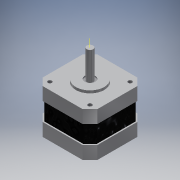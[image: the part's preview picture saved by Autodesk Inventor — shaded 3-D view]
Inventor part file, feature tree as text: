
AUTODESK INVENTOR PART (.ipt)
format: ipt  version: 2017 (Build 210142000, 142)  size: 289,792 bytes
history: native  units: mm
features: sketch x10, extrude x9, projected_geometry x8, mirror x4, plane x4, hole x1, other x1
ambient origin geometry x8: Origin, YZ Plane, XZ Plane, XY Plane, X Axis, Y Axis, Z Axis, Center Point
bodies: Solid1 (feature_tree)
feature tree (37):
  extrude  "Extrusion1"  Depth=40.3mm
  extrude  "Extrusion3"  Depth=34.0mm TaperAngle=0.0deg
  extrude  "Extrusion4"  Depth=2.0mm TaperAngle=0.0deg
  extrude  "Extrusion5"  Depth=1.0mm TaperAngle=0.0deg
  extrude  "Extrusion6"  Depth=22.0mm TaperAngle=0.0deg
  mirror  "Mirror1"
  extrude  "Extrusion7"  Depth=10.0mm
  mirror  "Mirror2"
  extrude  "Extrusion8"  Depth=10.0mm
  extrude  "Extrusion9"  Depth=10.0mm
  sketch  "Sketch15"  dims[d44=10.0mm d45=1.0mm d46=0.0mm]
  extrude  "Extrusion10"  Depth=1.0mm TaperAngle=0.0deg
  mirror  "Mirror3"
  mirror  "Mirror4"
  hole  "Hole3"  [1 undecoded]
  plane  "Work Plane4"
  sketch  "Sketch2"  dims[d2=30.0mm d3=40.3mm]
  sketch  "Sketch7"  dims[d4=135.0deg d5=34.0mm d6=0.0mm]
  sketch  "Sketch8"  dims[d27=22.0mm d28=2.0mm d29=0.0mm]
  sketch  "Sketch9"  dims[d30=8.0mm d31=1.0mm d32=0.0mm]
  sketch  "Sketch10"  dims[d33=5.0mm d34=22.0mm d35=0.0mm]
  projected_geometry  "Projected Loop2"
  sketch  "Sketch11"  dims[d36=10.0mm d37=10.0mm]
  projected_geometry  "Projected Loop3"
  sketch  "Sketch12"  dims[d38=1.0mm d39=0.0mm d40=10.0mm]
  projected_geometry  "Projected Loop4"
  sketch  "Sketch14"  dims[d41=1.0mm d42=0.0mm d43=10.0mm]
  projected_geometry  "Projected Loop6"
  projected_geometry  "Projected Loop7"
  projected_geometry  "Projected Loop8"
  projected_geometry  "Projected Loop9"
  plane  "Work Plane1"
  plane  "Work Plane2"
  plane  "Work Plane3"
  sketch  "Sketch17"  dims[d47=10.0mm d48=0.0mm d49=10.0mm d50=0.0mm d53=3.0mm d54=31.0mm d55=31.0mm d57=15.5mm d58=3.0mm d59=6.0mm d60=4.0mm d61=2.0mm d62=90.0deg d63=4.5mm d64=0.0mm d66=15.5mm d67=90.0deg]
  projected_geometry  "Projected Loop10"
  other  "Work Axis1"
note: 1 required parameter value undecoded (feature->parameter linkage not recoverable at this tier; creation-order binding heuristic only, values carry confidence <= 0.55)
